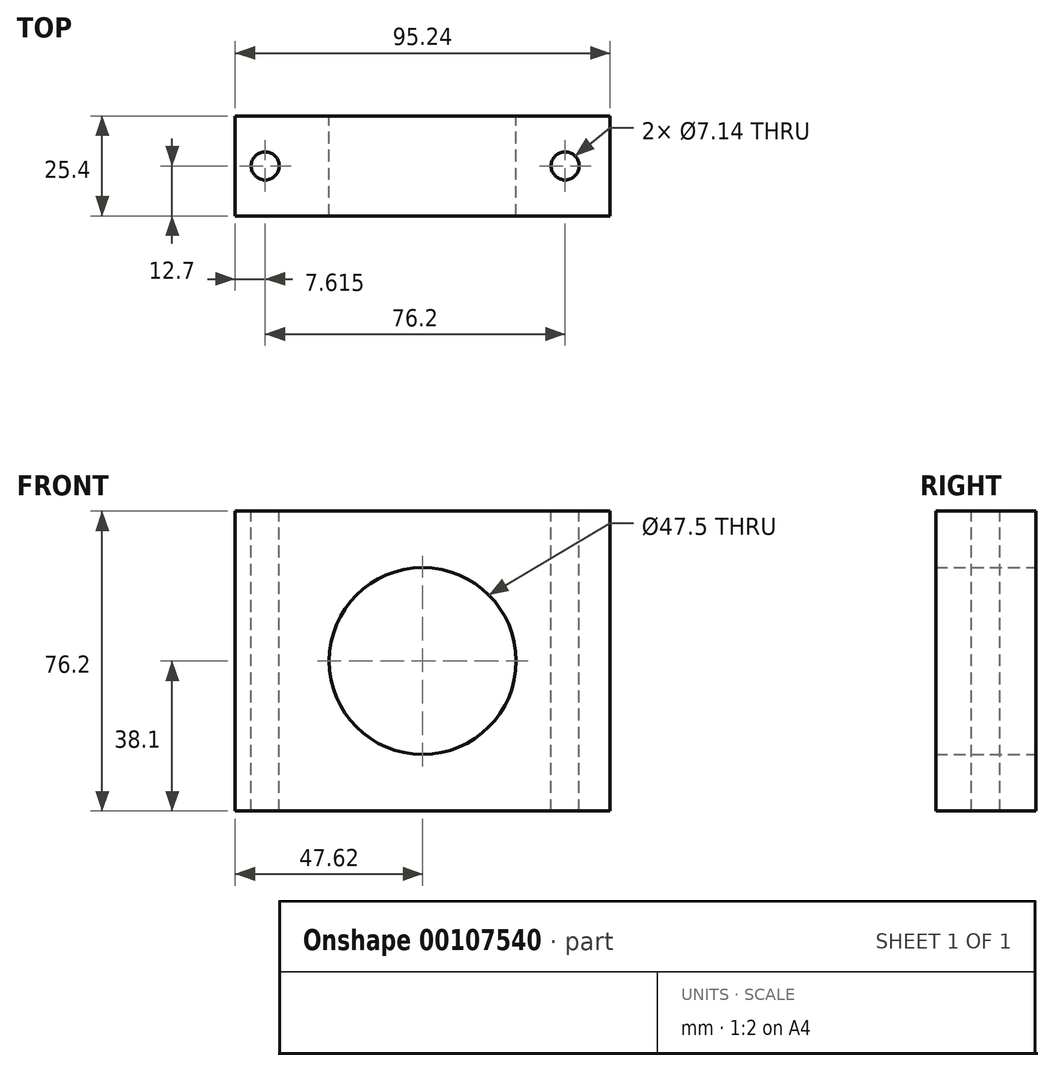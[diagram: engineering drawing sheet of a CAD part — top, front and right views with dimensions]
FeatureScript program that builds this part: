
annotation { "Feature Type Name" : "Feature", "Feature Type Description" : "" }
export const myFeature = defineFeature(function(context is Context, id is Id, definition is map)
    precondition{}
    {
        {
            var Q0;
            Q0=qCreatedBy(makeId("Front.planeOp"),FACE);
            var sketch = newSketch(context, id + "F0", { "sketchPlane" : qUnion([Q0])});
            skLineSegment(sketch, "E0.bottom", {"start": v(47.63, -38.1) * mm, "end": v(-47.63, -38.1) * mm});
            skLineSegment(sketch, "E0.top", {"start": v(47.63, 38.1) * mm, "end": v(-47.63, 38.1) * mm});
            skLineSegment(sketch, "E0.left", {"start": v(47.63, -38.1) * mm, "end": v(47.63, 38.1) * mm});
            skLineSegment(sketch, "E0.right", {"start": v(-47.63, -38.1) * mm, "end": v(-47.63, 38.1) * mm});
            skPoint(sketch, "E0.middle", {"position": v(0, 0) * mm});
            skLineSegment(sketch, "E1", {"start": v(-76.05, 0) * mm, "end": v(77.14, 0) * mm, "construction": true});
            skPoint(sketch, "E1.endSnap0", {"position": v(47.63, 0) * mm});
            skLineSegment(sketch, "E2", {"start": v(0, 76.77) * mm, "end": v(0, -76.43) * mm, "construction": true});
            skCircle(sketch, "E3", {"center": v(0, 0) * mm, "radius": 23.75 * mm});
            skSolve(sketch);
        }
        {
            var Q0;
            Q0 = qSketchRegion(id + "F0", true);
            extrude(context, id + "F1", {"entities" : qUnion([Q0]), "depth" : 25.4 * mm});
        }
        {
            var Q0;
            Q0=makeQuery(id+"F1.opExtrude","SWEPT_FACE",FACE,{"disambiguationData":[OSD([sQuery(id+"F0.wireOp",EDGE,"E0.top")])]});
            var sketch = newSketch(context, id + "F2", { "sketchPlane" : qUnion([Q0])});
            skLineSegment(sketch, "E4", {"start": v(0, 0) * mm, "end": v(0, -25.4) * mm, "construction": true});
            skLineSegment(sketch, "E5", {"start": v(-47.63, -12.7) * mm, "end": v(47.63, -12.7) * mm, "construction": true});
            skPoint(sketch, "E6", {"position": v(-40, -12.7) * mm});
            skPoint(sketch, "E7", {"position": v(36.2, -12.7) * mm});
            skPoint(sketch, "E8", {"position": v(47.63, 0) * mm});
            skCircle(sketch, "E9", {"center": v(-40, -12.7) * mm, "radius": 3.57 * mm});
            skCircle(sketch, "E10", {"center": v(36.2, -12.7) * mm, "radius": 3.57 * mm});
            skSolve(sketch);
        }
        {
            var Q0;
            Q0 = qSketchRegion(id + "F2", true);
            extrude(context, id + "F3", {"entities" : qUnion([Q0]), "operationType" : NewBodyOperationType.REMOVE, "endBound" : BoundingType.THROUGH_ALL, "oppositeDirection" : true, "depth" : 25.4 * mm});
        }
    });
